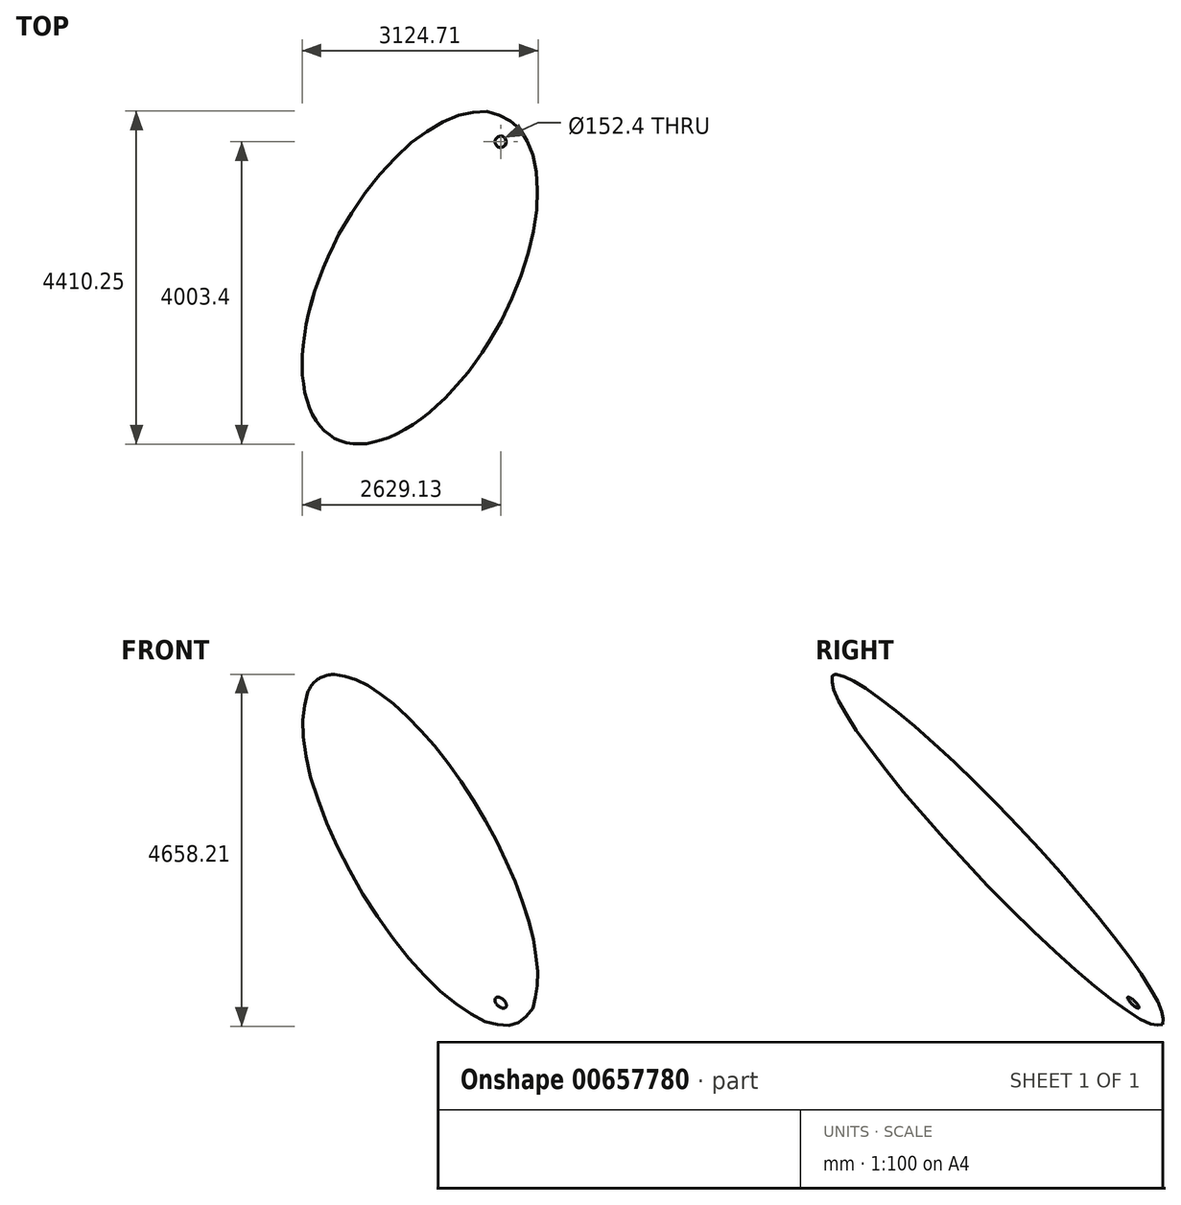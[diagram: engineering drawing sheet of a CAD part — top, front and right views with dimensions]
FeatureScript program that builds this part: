
annotation { "Feature Type Name" : "Feature", "Feature Type Description" : "" }
export const myFeature = defineFeature(function(context is Context, id is Id, definition is map)
    precondition{}
    {
        {
            assignVariable(context, id + "F0", {"name" : "Azimuth", "anyValue" : 298});
        }
        {
            assignVariable(context, id + "F1", {"name" : "Dip", "anyValue" : 44});
        }
        {
            assignVariable(context, id + "F2", {"name" : "Width", "anyValue" : .15});
        }
        {
            var Q0;
            Q0=qCreatedBy(makeId("Top.planeOp"),FACE);
            var sketch = newSketch(context, id + "F3", { "sketchPlane" : qUnion([Q0])});
            skEllipse(sketch, "E0", {"center": v(0, 0) * mm, "majorRadius": 1219.2 * mm, "minorRadius": 3352.8 * mm, "majorAxis": v(0, 1)});
            skLineSegment(sketch, "E1", {"start": v(0, 1219.2) * mm, "end": v(0, -1219.2) * mm, "construction": true});
            skLineSegment(sketch, "E2", {"start": v(-3352.8, 0) * mm, "end": v(3352.8, 0) * mm, "construction": true});
            skLineSegment(sketch, "E3.0", {"start": v(-1066.8, 1219.2) * mm, "end": v(-1066.8, -1219.2) * mm, "construction": true});
            skLineSegment(sketch, "E4.0", {"start": v(-3352.8, -1798.32) * mm, "end": v(3352.8, -1798.32) * mm, "construction": true});
            skSolve(sketch);
        }
        {
            var Q0;
            Q0=qCreatedBy(makeId("Top.planeOp"),FACE);
            var sketch = newSketch(context, id + "F4", { "sketchPlane" : qUnion([Q0])});
            skLineSegment(sketch, "E5", {"start": v(-1066.8, 0) * mm, "end": v(0, 0) * mm});
            skLineSegment(sketch, "E6", {"start": v(-1066.8, 0) * mm, "end": v(-1066.8, -1798.32) * mm});
            skSolve(sketch);
        }
        {
            var Q0;
            Q0=qSketchRegion(id+"F3",true);
            extrude(context, id + "F5", {"entities" : qUnion([Q0]), "depth" : (getVariable(context, 'Width')) * mm});
        }
        {
            var Q0;
            Q0=qCreatedBy(makeId("Front.planeOp"),FACE);
            var sketch = newSketch(context, id + "F6", { "sketchPlane" : qUnion([Q0])});
            skLineSegment(sketch, "E7", {"start": v(0, 0) * mm, "end": v(0, -6400.8) * mm, "construction": true});
            skSolve(sketch);
        }
        {
            var Q0;
            Q0=makeQuery(id+"F5.opExtrude","SWEPT_BODY",BODY,{"disambiguationData":[OSD([sQuery(id+"F3.wireOp",EDGE,"E0"),sQuery(id+"F3.wireOp",EDGE,"TMMzbr5i-4nV4-ZnMr-aG6B-IGJ66UyS6uPJ")])]});
            var Q1;
            Q1=sQuery(id+"F3.wireOp",EDGE,"E1");
            transform(context, id + "F7", {"entities" : qUnion([Q0]), "transformType" : TransformType.ROTATION, "transformAxis" : qUnion([Q1]), "angle" : (getVariable(context, 'Dip')) * degree, "oppositeDirection" : true, "makeCopy" : false});
        }
        {
            var Q0;
            Q0=makeQuery(id+"F5.opExtrude","SWEPT_BODY",BODY,{"disambiguationData":[OSD([sQuery(id+"F3.wireOp",EDGE,"E0")])]});
            var Q1;
            Q1=sQuery(id+"F6.wireOp",EDGE,"E7");
            transform(context, id + "F8", {"entities" : qUnion([Q0]), "transformType" : TransformType.ROTATION, "transformAxis" : qUnion([Q1]), "angle" : (getVariable(context, 'Azimuth')) * degree, "makeCopy" : false});
        }
        {
            var Q0;
            Q0=makeQuery(id+"F5.opExtrude","SWEPT_BODY",BODY,{"disambiguationData":[OSD([sQuery(id+"F3.wireOp",EDGE,"E0"),sQuery(id+"F3.wireOp",EDGE,"TMMzbr5i-4nV4-ZnMr-aG6B-IGJ66UyS6uPJ")])]});
            var Q1;
            Q1=sQuery(id+"F4.wireOp",EDGE,"E5");
            transform(context, id + "F9", {"entities" : qUnion([Q0]), "transformType" : TransformType.TRANSLATION_ENTITY, "oppositeDirectionEntity" : true, "transformLine" : qUnion([Q1]), "makeCopy" : false});
        }
        {
            var Q0;
            Q0=makeQuery(id+"F5.opExtrude","SWEPT_BODY",BODY,{"disambiguationData":[OSD([sQuery(id+"F3.wireOp",EDGE,"E0"),sQuery(id+"F3.wireOp",EDGE,"TMMzbr5i-4nV4-ZnMr-aG6B-IGJ66UyS6uPJ")])]});
            var Q1;
            Q1=sQuery(id+"F4.wireOp",EDGE,"E6");
            transform(context, id + "F10", {"entities" : qUnion([Q0]), "transformType" : TransformType.TRANSLATION_ENTITY, "oppositeDirectionEntity" : false, "transformLine" : qUnion([Q1]), "makeCopy" : false});
        }
        {
            var Q0;
            Q0=qCreatedBy(makeId("Top.planeOp"),FACE);
            var sketch = newSketch(context, id + "F11", { "sketchPlane" : qUnion([Q0])});
            skCircle(sketch, "E8", {"center": v(0, 0) * mm, "radius": 76.2 * mm});
            skSolve(sketch);
        }
        {
            var Q0;
            Q0=qSketchRegion(id+"F11",true);
            extrude(context, id + "F12", {"entities" : qUnion([Q0]), "operationType" : NewBodyOperationType.REMOVE, "endBound" : BoundingType.THROUGH_ALL, "oppositeDirection" : true, "depth" : 30.48 * mm, "hasSecondDirection" : true, "secondDirectionBound" : SecondDirectionBoundingType.THROUGH_ALL, "secondDirectionOppositeDirection" : false, "secondDirectionDepth" : 30.48 * mm});
        }
        {
            var Q0;
            Q0=qCreatedBy(makeId("Front.planeOp"),FACE);
            var sketch = newSketch(context, id + "F13", { "sketchPlane" : qUnion([Q0])});
            skLineSegment(sketch, "E9", {"start": v(0, -2010.63) * mm, "end": v(0, -6400.8) * mm});
            skSolve(sketch);
        }
        {
            var Q0;
            Q0=makeQuery(id+"F5.opExtrude","SWEPT_BODY",BODY,{"disambiguationData":[OSD([sQuery(id+"F3.wireOp",EDGE,"E0")])]});
            var Q1;
            Q1=sQuery(id+"F13.wireOp",EDGE,"E9");
            transform(context, id + "F14", {"entities" : qUnion([Q0]), "transformType" : TransformType.TRANSLATION_ENTITY, "oppositeDirectionEntity" : false, "transformLine" : qUnion([Q1]), "makeCopy" : false});
        }
    });
